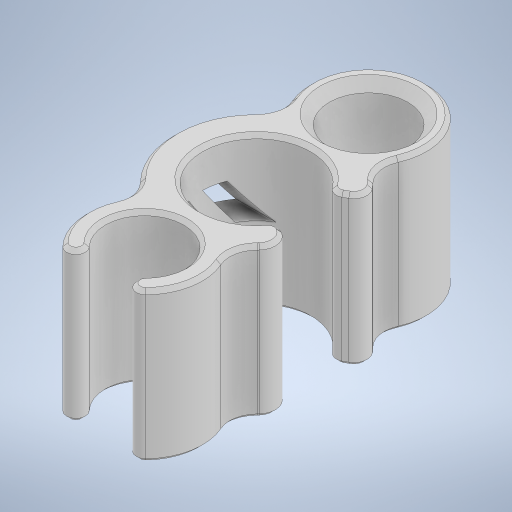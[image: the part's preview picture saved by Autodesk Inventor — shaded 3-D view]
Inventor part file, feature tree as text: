
AUTODESK INVENTOR PART (.ipt)
format: ipt  version: 2024.2 (Build 282272000, 272)  size: 388,096 bytes
history: native  units: mm
features: fillet x5, extrude x2, chamfer x2, sketch x2, plane x1
ambient origin geometry x8: Origin, YZ Plane, XZ Plane, XY Plane, X Axis, Y Axis, Z Axis, Center Point
bodies: Solid1 (feature_tree)
feature tree (12):
  extrude  "Extrusion1"  Depth=1.5mm
  fillet  "Fillet1"  Radius=4.2mm
  fillet  "Fillet2"  Radius=6.0mm
  fillet  "Fillet3"  Radius=6.0mm
  fillet  "Fillet4"  Radius=1.5mm
  fillet  "Fillet5"  Radius=1.0mm
  plane  "Work Plane1"
  extrude  "Extrusion2"  Depth=8.0mm TaperAngle=0.0deg
  chamfer  "Chamfer1"  Distance=2.8mm
  chamfer  "Chamfer2"  Distance=1.4mm
  sketch  "Sketch1"  dims[d0=5.8mm d1=4.2mm d2=4.2mm d3=6.0mm d4=6.0mm d5=1.5mm d6=1.0mm]
  sketch  "Sketch2"  dims[d7=1.0mm d8=8.0mm d9=0.0mm d10=2.8mm d11=1.4mm d12=1.5mm d13=2.4mm d14=1.2mm d15=0.9mm d16=0.5mm d17=0.7mm d18=0.5mm d19=21.816616mm d20=4.0mm d21=5.0mm d22=0.85mm d23=2.5mm d24=2.0mm d26=8.0mm d27=0.0mm d28=0.5mm d29=2.0mm d30=45.0deg d31=0.2mm d32=2.0mm d33=45.0deg]
